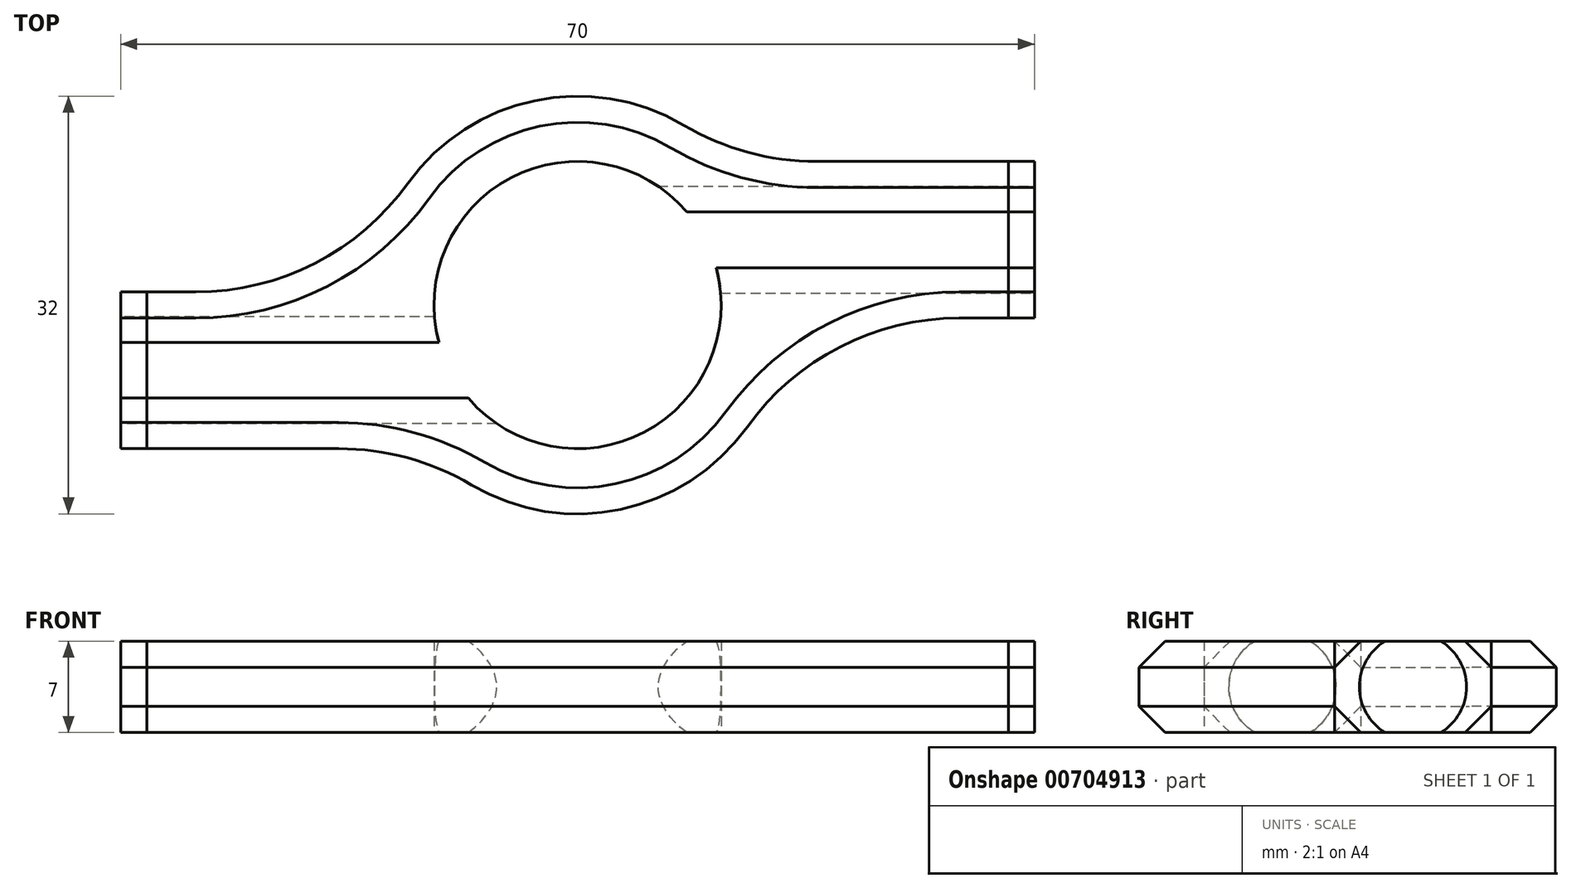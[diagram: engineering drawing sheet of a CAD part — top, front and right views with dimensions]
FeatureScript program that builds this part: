
annotation { "Feature Type Name" : "Feature", "Feature Type Description" : "" }
export const myFeature = defineFeature(function(context is Context, id is Id, definition is map)
    precondition{}
    {
        {
            var Q0;
            Q0=qCreatedBy(makeId("Top.planeOp"),FACE);
            var sketch = newSketch(context, id + "F0", { "sketchPlane" : qUnion([Q0])});
            skCircle(sketch, "E0", {"center": v(0, 0) * mm, "radius": 11 * mm});
            skLineSegment(sketch, "E1.anchor1", {"start": v(0, 15.99) * mm, "end": v(0, 0) * mm, "construction": true});
            skLineSegment(sketch, "E1.anchor2", {"start": v(0, 0) * mm, "end": v(-49.82, 0) * mm, "construction": true});
            skArc(sketch, "E2", {"start": v(11.62, 11) * mm, "mid": v(-5.45, 15.04) * mm, "end": v(-15.97, 1) * mm});
            skLineSegment(sketch, "E3", {"start": v(0, 11) * mm, "end": v(0, 11) * mm});
            skLineSegment(sketch, "E4", {"start": v(35, 11) * mm, "end": v(35, -1) * mm});
            skLineSegment(sketch, "E5", {"start": v(35, -1) * mm, "end": v(15.97, -1) * mm});
            skLineSegment(sketch, "E6.1.0", {"start": v(-11.62, -11) * mm, "end": v(-35, -11) * mm});
            skLineSegment(sketch, "E6.1.1", {"start": v(-35, -11) * mm, "end": v(-35, 1) * mm});
            skLineSegment(sketch, "E6.1.2", {"start": v(-35, 1) * mm, "end": v(-15.97, 1) * mm});
            skLineSegment(sketch, "E7.trimOffspring", {"start": v(11.62, 11) * mm, "end": v(35, 11) * mm});
            skArc(sketch, "E8.trimOffspring", {"start": v(-11.62, -11) * mm, "mid": v(5.45, -15.04) * mm, "end": v(15.97, -1) * mm});
            skPoint(sketch, "E9.orphan", {"position": v(0, -11) * mm});
            skSolve(sketch);
        }
        {
            var Q0;
            Q0 = qSketchRegion(id + "F0", true);
            extrude(context, id + "F1", {"entities" : qUnion([Q0]), "depth" : 7 * mm, "offsetDistance" : 25 * mm});
        }
        {
            var Q0;
            Q0=makeQuery(id+"F1.opExtrude","SWEPT_FACE",FACE,{"disambiguationData":[OSD([sQuery(id+"F0.wireOp",EDGE,"E4")])]});
            var sketch = newSketch(context, id + "F2", { "sketchPlane" : qUnion([Q0])});
            skLineSegment(sketch, "E10", {"start": v(11, 7) * mm, "end": v(-1, 0) * mm, "construction": true});
            skCircle(sketch, "E11", {"center": v(5, 3.5) * mm, "radius": 4.1 * mm});
            skSolve(sketch);
        }
        {
            var Q0;
            Q0 = qSketchRegion(id + "F2", true);
            extrude(context, id + "F3", {"entities" : qUnion([Q0]), "operationType" : NewBodyOperationType.REMOVE, "endBound" : BoundingType.UP_TO_NEXT, "oppositeDirection" : true, "depth" : 43.6 * mm, "offsetDistance" : 25 * mm});
        }
        {
            var Q0;
            Q0=makeQuery(id+"F1.opExtrude","SWEPT_FACE",FACE,{"disambiguationData":[OSD([sQuery(id+"F0.wireOp",EDGE,"E6.1.1")])]});
            var sketch = newSketch(context, id + "F4", { "sketchPlane" : qUnion([Q0])});
            skLineSegment(sketch, "E12", {"start": v(-1, 0) * mm, "end": v(11, 7) * mm, "construction": true});
            skCircle(sketch, "E13", {"center": v(5, 3.5) * mm, "radius": 4.1 * mm});
            skSolve(sketch);
        }
        {
            var Q0;
            Q0 = qSketchRegion(id + "F4", true);
            extrude(context, id + "F5", {"entities" : qUnion([Q0]), "operationType" : NewBodyOperationType.REMOVE, "endBound" : BoundingType.UP_TO_NEXT, "oppositeDirection" : true, "depth" : 25 * mm, "offsetDistance" : 25 * mm});
        }
        {
            var Q0;
            {var subQ1=sQuery(id+"F0.wireOp",EDGE,"E7.trimOffspring");var subQ6=sQuery(id+"F0.wireOp",EDGE,"E4");Q0=makeQuery(id+"F3.boolean.opBoolean","SPLIT",FACE,{"disambiguationData":[TD([makeQuery(id+"F1.opExtrude","SWEPT_FACE",FACE,{"disambiguationData":[OSD([subQ1])]})])],"derivedFrom":makeQuery(id+"F1.opExtrude","SWEPT_FACE",FACE,{"disambiguationData":[OSD([subQ6])]})});}
            var sketch = newSketch(context, id + "F6", { "sketchPlane" : qUnion([Q0])});
            skLineSegment(sketch, "E14.0", {"start": v(11, 7) * mm, "end": v(11, 0) * mm});
            skLineSegment(sketch, "E14.1", {"start": v(-1, 7) * mm, "end": v(-1, 0) * mm});
            skLineSegment(sketch, "E15", {"start": v(11, 7) * mm, "end": v(-1, 7) * mm});
            skLineSegment(sketch, "E16", {"start": v(11, 0) * mm, "end": v(-1, 0) * mm});
            skSolve(sketch);
        }
        {
            var Q0;
            Q0 = qSketchRegion(id + "F6", true);
            extrude(context, id + "F7", {"entities" : qUnion([Q0]), "oppositeDirection" : true, "depth" : 2 * mm, "offsetDistance" : 25 * mm});
        }
        {
            var Q0;
            {var subQ0=sQuery(id+"F0.wireOp",EDGE,"E6.1.2");var subQ1=sQuery(id+"F0.wireOp",EDGE,"E6.1.1");Q0=makeQuery(id+"F5.boolean.opBoolean","SPLIT",FACE,{"disambiguationData":[TD([makeQuery(id+"F1.opExtrude","SWEPT_FACE",FACE,{"disambiguationData":[OSD([subQ0])]})])],"derivedFrom":makeQuery(id+"F1.opExtrude","SWEPT_FACE",FACE,{"disambiguationData":[OSD([subQ1])]})});}
            var sketch = newSketch(context, id + "F8", { "sketchPlane" : qUnion([Q0])});
            skLineSegment(sketch, "E17.0", {"start": v(-1, 7) * mm, "end": v(-1, 0) * mm});
            skLineSegment(sketch, "E17.1", {"start": v(11, 7) * mm, "end": v(11, 0) * mm});
            skLineSegment(sketch, "E18", {"start": v(-1, 0) * mm, "end": v(11, 0) * mm});
            skLineSegment(sketch, "E19", {"start": v(-1, 7) * mm, "end": v(11, 7) * mm});
            skSolve(sketch);
        }
        {
            var Q0;
            Q0 = qSketchRegion(id + "F8", true);
            extrude(context, id + "F9", {"entities" : qUnion([Q0]), "oppositeDirection" : true, "depth" : 2 * mm, "offsetDistance" : 25 * mm});
        }
        {
            var Q0;
            Q0=makeQuery(id+"F1.opExtrude","SWEPT_EDGE",EDGE,{"disambiguationData":[OSD([sQuery(id+"F0.wireOp",EDGE,"E2"),sQuery(id+"F0.wireOp",EDGE,"E7.trimOffspring")])]});
            var Q1;
            Q1=makeQuery(id+"F1.opExtrude","SWEPT_EDGE",EDGE,{"disambiguationData":[OSD([sQuery(id+"F0.wireOp",EDGE,"E2"),sQuery(id+"F0.wireOp",EDGE,"E6.1.2")])]});
            var Q2;
            Q2=makeQuery(id+"F1.opExtrude","SWEPT_EDGE",EDGE,{"disambiguationData":[OSD([sQuery(id+"F0.wireOp",EDGE,"E5"),sQuery(id+"F0.wireOp",EDGE,"E8.trimOffspring")])]});
            var Q3;
            Q3=makeQuery(id+"F1.opExtrude","SWEPT_EDGE",EDGE,{"disambiguationData":[OSD([sQuery(id+"F0.wireOp",EDGE,"E6.1.0"),sQuery(id+"F0.wireOp",EDGE,"E8.trimOffspring")])]});
            fillet(context, id + "F10", {"entities" : qUnion([Q0, Q1, Q2, Q3]), "radius" : 20 * mm, "tangentPropagation" : true, "allowEdgeOverflow" : false});
        }
        {
            var Q0;
            Q0=makeQuery(id+"F1.opExtrude","CAP_EDGE",EDGE,{"disambiguationData":[OSD([sQuery(id+"F0.wireOp",EDGE,"E6.1.0")])],"isStart":false});
            var Q1;
            {var subQ0=sQuery(id+"F0.wireOp",EDGE,"E2");Q1=makeQuery(id+"F1.opExtrude","CAP_EDGE",EDGE,{"disambiguationData":[OSD([subQ0]),TDD([makeQuery(id+"F0.imprint","IMPRINT",EDGE,{"disambiguationData":[TD([[makeQuery(id+"F0.imprint","INTERSECT",VERTEX,{"derivedFrom":[subQ0,sQuery(id+"F0.wireOp",EDGE,"E5")]}),1.0]])],"derivedFrom":subQ0})])],"isStart":false});}
            var Q2;
            Q2=makeQuery(id+"F1.opExtrude","CAP_EDGE",EDGE,{"disambiguationData":[OSD([sQuery(id+"F0.wireOp",EDGE,"E5")])],"isStart":false});
            var Q3;
            Q3=makeQuery(id+"F1.opExtrude","CAP_EDGE",EDGE,{"disambiguationData":[OSD([sQuery(id+"F0.wireOp",EDGE,"E3")])],"isStart":false});
            var Q4;
            {var subQ0=sQuery(id+"F0.wireOp",EDGE,"E2");Q4=makeQuery(id+"F1.opExtrude","CAP_EDGE",EDGE,{"disambiguationData":[OSD([subQ0]),TDD([makeQuery(id+"F0.imprint","IMPRINT",EDGE,{"disambiguationData":[TD([[makeQuery(id+"F0.imprint","INTERSECT",VERTEX,{"derivedFrom":[subQ0,sQuery(id+"F0.wireOp",EDGE,"E6.1.2")]}),1.0]])],"derivedFrom":subQ0})])],"isStart":false});}
            var Q5;
            Q5=makeQuery(id+"F1.opExtrude","CAP_EDGE",EDGE,{"disambiguationData":[OSD([sQuery(id+"F0.wireOp",EDGE,"E6.1.2")])],"isStart":false});
            var Q6;
            Q6=makeQuery(id+"F1.opExtrude","CAP_EDGE",EDGE,{"disambiguationData":[OSD([sQuery(id+"F0.wireOp",EDGE,"E5")])],"isStart":true});
            var Q7;
            Q7=makeQuery(id+"F1.opExtrude","CAP_EDGE",EDGE,{"disambiguationData":[OSD([sQuery(id+"F0.wireOp",EDGE,"E3")])],"isStart":true});
            var Q8;
            {var subQ0=sQuery(id+"F0.wireOp",EDGE,"E2");Q8=makeQuery(id+"F1.opExtrude","CAP_EDGE",EDGE,{"disambiguationData":[OSD([subQ0]),TDD([makeQuery(id+"F0.imprint","IMPRINT",EDGE,{"disambiguationData":[TD([[makeQuery(id+"F0.imprint","INTERSECT",VERTEX,{"derivedFrom":[subQ0,sQuery(id+"F0.wireOp",EDGE,"E6.1.2")]}),1.0]])],"derivedFrom":subQ0})])],"isStart":true});}
            var Q9;
            {var subQ0=sQuery(id+"F0.wireOp",EDGE,"E2");Q9=makeQuery(id+"F1.opExtrude","CAP_EDGE",EDGE,{"disambiguationData":[OSD([subQ0]),TDD([makeQuery(id+"F0.imprint","IMPRINT",EDGE,{"disambiguationData":[TD([[makeQuery(id+"F0.imprint","INTERSECT",VERTEX,{"derivedFrom":[subQ0,sQuery(id+"F0.wireOp",EDGE,"E5")]}),1.0]])],"derivedFrom":subQ0})])],"isStart":true});}
            var Q10;
            Q10=makeQuery(id+"F1.opExtrude","CAP_EDGE",EDGE,{"disambiguationData":[OSD([sQuery(id+"F0.wireOp",EDGE,"E6.1.0")])],"isStart":true});
            var Q11;
            Q11=makeQuery(id+"F1.opExtrude","CAP_EDGE",EDGE,{"disambiguationData":[OSD([sQuery(id+"F0.wireOp",EDGE,"E6.1.2")])],"isStart":true});
            chamfer(context, id + "F11", {"entities" : qUnion([Q0, Q1, Q2, Q3, Q4, Q5, Q6, Q7, Q8, Q9, Q10, Q11]), "width" : 2 * mm, "tangentPropagation" : true});
        }
    });
